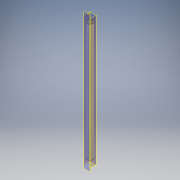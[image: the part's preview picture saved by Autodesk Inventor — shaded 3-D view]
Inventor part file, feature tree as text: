
AUTODESK INVENTOR PART (.ipt)
format: ipt  version: 2018 (Build 220112000, 112)  size: 96,256 bytes
history: native  units: mm
features: other x5, extrude x1, sketch x1
ambient origin geometry x8: Origin, YZ Plane, XZ Plane, XY Plane, X Axis, Y Axis, Z Axis, Center Point
bodies: Body1 (feature_tree)
feature tree (7):
  other  "ソリッド1"
  extrude  "押し出し1"  Depth=27.2mm
  other  "作業平面3"
  other  "作業平面4"
  other  "作業平面5"
  other  "作業平面6"
  sketch  "スケッチ1"
